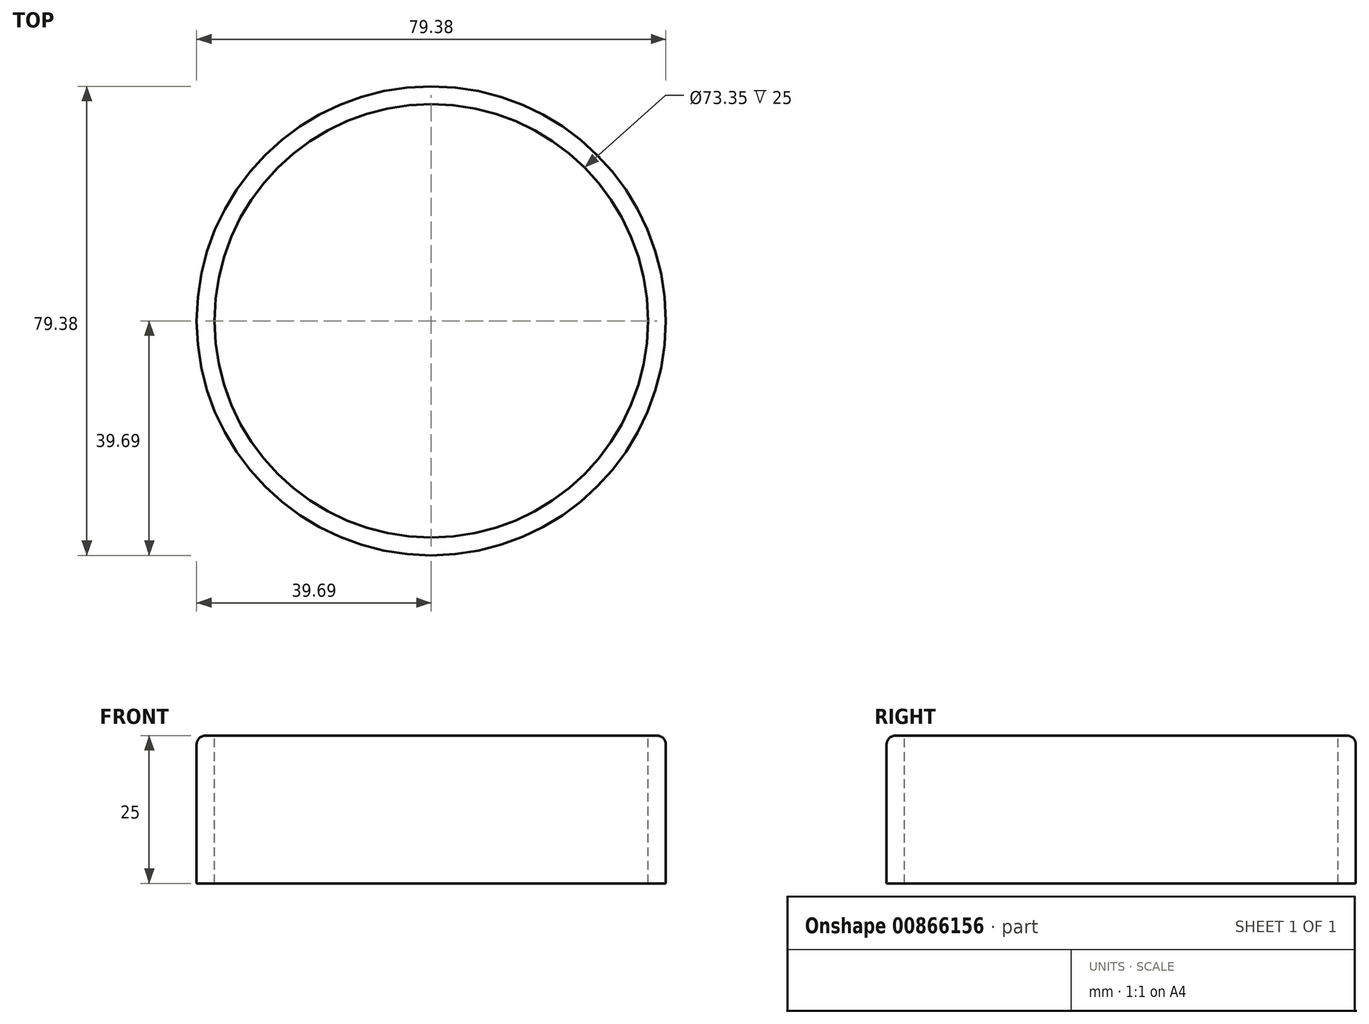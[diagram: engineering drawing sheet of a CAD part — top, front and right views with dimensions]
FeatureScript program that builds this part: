
annotation { "Feature Type Name" : "Feature", "Feature Type Description" : "" }
export const myFeature = defineFeature(function(context is Context, id is Id, definition is map)
    precondition{}
    {
        {
            var Q0;
            Q0=qCreatedBy(makeId("Top.planeOp"),FACE);
            var sketch = newSketch(context, id + "F0", { "sketchPlane" : qUnion([Q0])});
            skCircle(sketch, "E0", {"center": v(0, 0) * mm, "radius": 39.69 * mm});
            skSolve(sketch);
        }
        {
            var Q0;
            Q0=makeQuery(id+"F0.imprint","IMPRINT",FACE,{"disambiguationData":[TD([[makeQuery(id+"F0.imprint","IMPRINT",EDGE,{"derivedFrom":sQuery(id+"F0.wireOp",EDGE,"E0")}),1.0]])]});
            extrude(context, id + "F1", {"entities" : qUnion([Q0]), "depth" : 25 * mm, "offsetDistance" : 25 * mm});
        }
        {
            var Q0;
            Q0=makeQuery(id+"F1.opExtrude","CAP_FACE",FACE,{"disambiguationData":[OSD([sQuery(id+"F0.wireOp",EDGE,"E0")])],"isStart":false});
            var sketch = newSketch(context, id + "F2", { "sketchPlane" : qUnion([Q0])});
            skCircle(sketch, "E1.0", {"center": v(0, 0) * mm, "radius": 36.68 * mm});
            skSolve(sketch);
        }
        {
            var Q0;
            Q0 = qSketchRegion(id + "F2", true);
            extrude(context, id + "F3", {"entities" : qUnion([Q0]), "operationType" : NewBodyOperationType.REMOVE, "oppositeDirection" : true, "depth" : 25 * mm, "offsetDistance" : 25 * mm});
        }
        {
            var Q0;
            Q0=makeQuery(id+"F3.boolean.opBoolean","COPY",EDGE,{"derivedFrom":makeQuery(id+"F3.opExtrude","CAP_EDGE",EDGE,{"disambiguationData":[OSD([sQuery(id+"F2.wireOp",EDGE,"E1.0")])],"isStart":true})});
            var Q1;
            Q1=makeQuery(id+"F1.opExtrude","CAP_EDGE",EDGE,{"disambiguationData":[OSD([sQuery(id+"F0.wireOp",EDGE,"E0")])],"isStart":false});
            fillet(context, id + "F4", {"entities" : qUnion([Q0, Q1]), "radius" : 1.5 * mm, "tangentPropagation" : true, "allowEdgeOverflow" : false});
        }
    });
